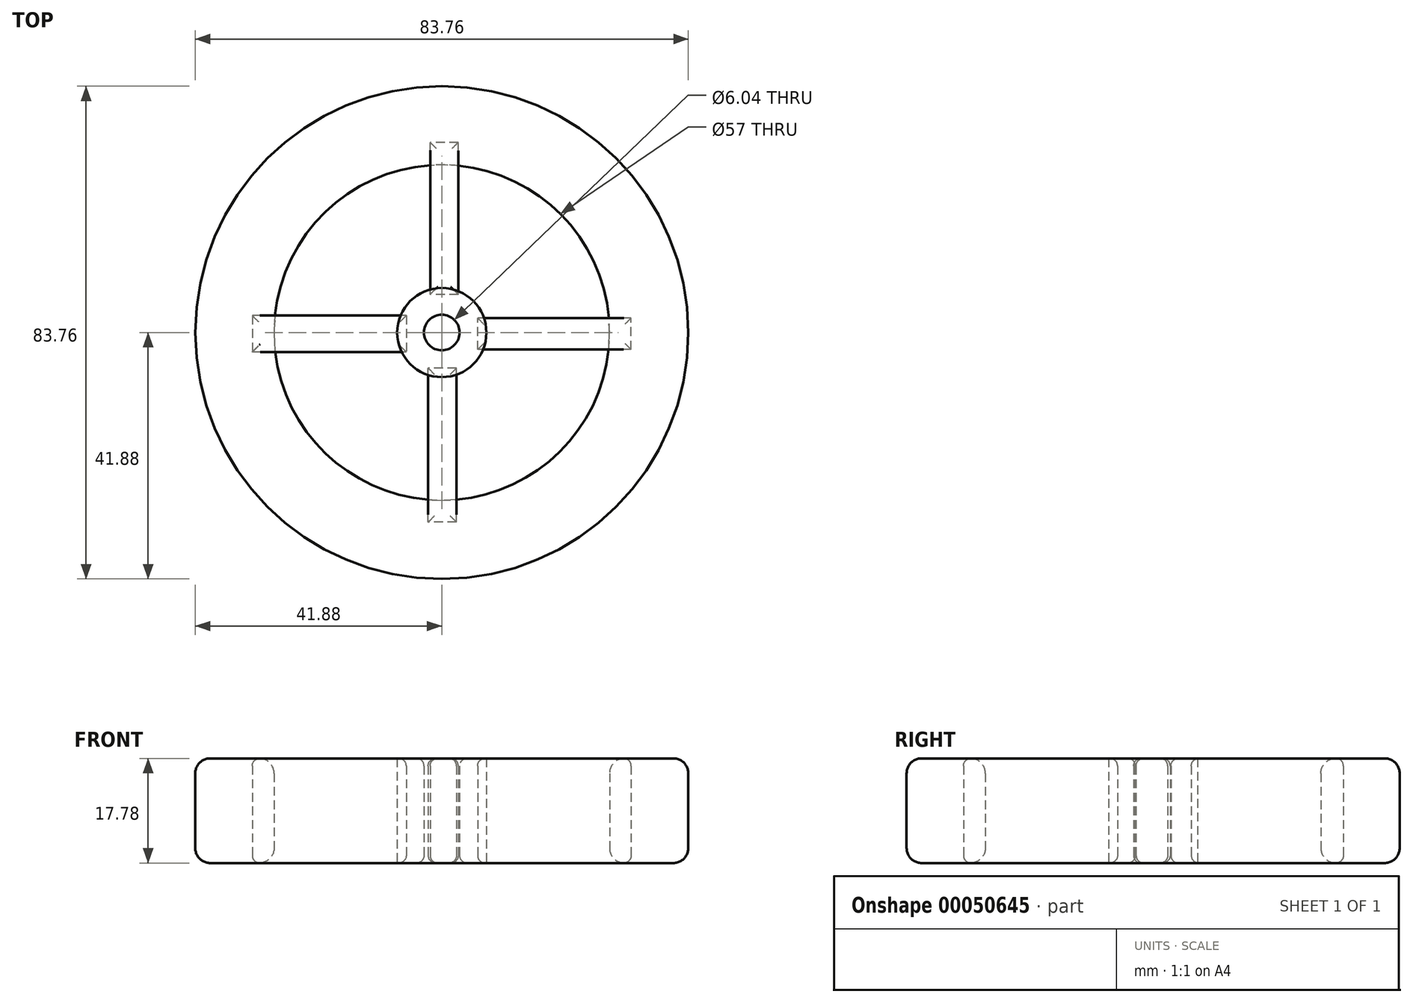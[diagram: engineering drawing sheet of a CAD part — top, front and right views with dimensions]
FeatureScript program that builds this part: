
annotation { "Feature Type Name" : "Feature", "Feature Type Description" : "" }
export const myFeature = defineFeature(function(context is Context, id is Id, definition is map)
    precondition{}
    {
        {
            var Q0;
            Q0=qCreatedBy(makeId("Top.planeOp"),FACE);
            var sketch = newSketch(context, id + "F0", { "sketchPlane" : qUnion([Q0])});
            skCircle(sketch, "E0", {"center": v(0, 0) * mm, "radius": 41.88 * mm});
            skCircle(sketch, "E1", {"center": v(0, 0) * mm, "radius": 22.29 * mm});
            skCircle(sketch, "E2", {"center": v(0, 0) * mm, "radius": 28.5 * mm});
            skSolve(sketch);
        }
        {
            var Q0;
            Q0=makeQuery(id+"F0.imprint","IMPRINT",FACE,{"disambiguationData":[TD([[makeQuery(id+"F0.imprint","IMPRINT",EDGE,{"derivedFrom":sQuery(id+"F0.wireOp",EDGE,"E0")}),1.0]])]});
            extrude(context, id + "F1", {"entities" : qUnion([Q0]), "depth" : 17.78 * mm});
        }
        {
            var Q0;
            Q0=qCreatedBy(makeId("Top.planeOp"),FACE);
            var sketch = newSketch(context, id + "F2", { "sketchPlane" : qUnion([Q0])});
            skCircle(sketch, "E3", {"center": v(0, 0) * mm, "radius": 7.58 * mm});
            skCircle(sketch, "E4", {"center": v(0, 0) * mm, "radius": 3.02 * mm});
            skSolve(sketch);
        }
        {
            var Q0;
            Q0=makeQuery(id+"F2.imprint","IMPRINT",FACE,{"disambiguationData":[TD([[makeQuery(id+"F2.imprint","IMPRINT",EDGE,{"derivedFrom":sQuery(id+"F2.wireOp",EDGE,"E3")}),1.0]])]});
            extrude(context, id + "F3", {"entities" : qUnion([Q0]), "depth" : 17.78 * mm});
        }
        {
            var Q0;
            Q0=qCreatedBy(makeId("Top.planeOp"),FACE);
            var sketch = newSketch(context, id + "F4", { "sketchPlane" : qUnion([Q0])});
            skLineSegment(sketch, "E5.bottom", {"start": v(2.5, -32.22) * mm, "end": v(-2.32, -32.22) * mm});
            skLineSegment(sketch, "E5.top", {"start": v(2.5, -6.05) * mm, "end": v(-2.32, -6.05) * mm});
            skLineSegment(sketch, "E5.left", {"start": v(2.5, -32.22) * mm, "end": v(2.5, -6.05) * mm});
            skLineSegment(sketch, "E5.right", {"start": v(-2.32, -32.22) * mm, "end": v(-2.32, -6.05) * mm});
            skSolve(sketch);
        }
        {
            var Q0;
            Q0=makeQuery(id+"F4.imprint","IMPRINT",FACE,{"disambiguationData":[TD([[makeQuery(id+"F4.imprint","IMPRINT",EDGE,{"derivedFrom":sQuery(id+"F4.wireOp",EDGE,"E5.bottom")}),-1.0]])]});
            extrude(context, id + "F5", {"entities" : qUnion([Q0]), "depth" : 17.78 * mm});
        }
        {
            var Q0;
            Q0=qCreatedBy(makeId("Top.planeOp"),FACE);
            var sketch = newSketch(context, id + "F6", { "sketchPlane" : qUnion([Q0])});
            skLineSegment(sketch, "E6.bottom", {"start": v(2.8, 6.48) * mm, "end": v(-1.98, 6.48) * mm});
            skLineSegment(sketch, "E6.top", {"start": v(2.8, 32.33) * mm, "end": v(-1.98, 32.33) * mm});
            skLineSegment(sketch, "E6.left", {"start": v(2.8, 6.48) * mm, "end": v(2.8, 32.33) * mm});
            skLineSegment(sketch, "E6.right", {"start": v(-1.98, 6.48) * mm, "end": v(-1.98, 32.33) * mm});
            skSolve(sketch);
        }
        {
            var Q0;
            Q0=makeQuery(id+"F6.imprint","IMPRINT",FACE,{"disambiguationData":[TD([[makeQuery(id+"F6.imprint","IMPRINT",EDGE,{"derivedFrom":sQuery(id+"F6.wireOp",EDGE,"E6.bottom")}),-1.0]])]});
            extrude(context, id + "F7", {"entities" : qUnion([Q0]), "depth" : 17.78 * mm});
        }
        {
            var Q0;
            Q0=qCreatedBy(makeId("Top.planeOp"),FACE);
            var sketch = newSketch(context, id + "F8", { "sketchPlane" : qUnion([Q0])});
            skLineSegment(sketch, "E7.bottom", {"start": v(-6.03, 2.9) * mm, "end": v(-32.2, 2.9) * mm});
            skLineSegment(sketch, "E7.top", {"start": v(-6.03, -3.3) * mm, "end": v(-32.2, -3.3) * mm});
            skLineSegment(sketch, "E7.left", {"start": v(-6.03, 2.9) * mm, "end": v(-6.03, -3.3) * mm});
            skLineSegment(sketch, "E7.right", {"start": v(-32.2, 2.9) * mm, "end": v(-32.2, -3.3) * mm});
            skSolve(sketch);
        }
        {
            var Q0;
            Q0=makeQuery(id+"F8.imprint","IMPRINT",FACE,{"disambiguationData":[TD([[makeQuery(id+"F8.imprint","IMPRINT",EDGE,{"derivedFrom":sQuery(id+"F8.wireOp",EDGE,"E7.bottom")}),1.0]])]});
            extrude(context, id + "F9", {"entities" : qUnion([Q0]), "depth" : 17.78 * mm});
        }
        {
            var Q0;
            Q0=qCreatedBy(makeId("Top.planeOp"),FACE);
            var sketch = newSketch(context, id + "F10", { "sketchPlane" : qUnion([Q0])});
            skLineSegment(sketch, "E8.bottom", {"start": v(32.17, -2.9) * mm, "end": v(6.08, -2.9) * mm});
            skLineSegment(sketch, "E8.top", {"start": v(32.17, 2.48) * mm, "end": v(6.08, 2.48) * mm});
            skLineSegment(sketch, "E8.left", {"start": v(32.17, -2.9) * mm, "end": v(32.17, 2.48) * mm});
            skLineSegment(sketch, "E8.right", {"start": v(6.08, -2.9) * mm, "end": v(6.08, 2.48) * mm});
            skSolve(sketch);
        }
        {
            var Q0;
            Q0=makeQuery(id+"F10.imprint","IMPRINT",FACE,{"disambiguationData":[TD([[makeQuery(id+"F10.imprint","IMPRINT",EDGE,{"derivedFrom":sQuery(id+"F10.wireOp",EDGE,"E8.bottom")}),-1.0]])]});
            extrude(context, id + "F11", {"entities" : qUnion([Q0]), "depth" : 17.78 * mm});
        }
        {
            var Q0;
            Q0=makeQuery(id+"F1.opExtrude","CAP_FACE",FACE,{"disambiguationData":[OSD([sQuery(id+"F0.wireOp",EDGE,"E0"),sQuery(id+"F0.wireOp",EDGE,"E2")])],"isStart":false});
            fillet(context, id + "F12", {"entities" : qUnion([Q0]), "radius" : 2.54 * mm, "tangentPropagation" : true, "allowEdgeOverflow" : false});
        }
        {
            var Q0;
            Q0=makeQuery(id+"F1.opExtrude","CAP_FACE",FACE,{"disambiguationData":[OSD([sQuery(id+"F0.wireOp",EDGE,"E0"),sQuery(id+"F0.wireOp",EDGE,"E2")])],"isStart":true});
            fillet(context, id + "F13", {"entities" : qUnion([Q0]), "radius" : 2.54 * mm, "tangentPropagation" : true, "allowEdgeOverflow" : false});
        }
        {
            var Q0;
            Q0=makeQuery(id+"F9.opExtrude","CAP_FACE",FACE,{"disambiguationData":[OSD([sQuery(id+"F8.wireOp",EDGE,"E7.bottom"),sQuery(id+"F8.wireOp",EDGE,"E7.top"),sQuery(id+"F8.wireOp",EDGE,"E7.left"),sQuery(id+"F8.wireOp",EDGE,"E7.right")])],"isStart":false});
            fillet(context, id + "F14", {"entities" : qUnion([Q0]), "radius" : 1.27 * mm, "tangentPropagation" : true, "allowEdgeOverflow" : false});
        }
        {
            var Q0;
            Q0=makeQuery(id+"F9.opExtrude","CAP_FACE",FACE,{"disambiguationData":[OSD([sQuery(id+"F8.wireOp",EDGE,"E7.bottom"),sQuery(id+"F8.wireOp",EDGE,"E7.top"),sQuery(id+"F8.wireOp",EDGE,"E7.left"),sQuery(id+"F8.wireOp",EDGE,"E7.right")])],"isStart":true});
            fillet(context, id + "F15", {"entities" : qUnion([Q0]), "radius" : 1.27 * mm, "tangentPropagation" : true, "allowEdgeOverflow" : false});
        }
        {
            var Q0;
            Q0=makeQuery(id+"F7.opExtrude","CAP_FACE",FACE,{"disambiguationData":[OSD([sQuery(id+"F6.wireOp",EDGE,"E6.bottom"),sQuery(id+"F6.wireOp",EDGE,"E6.top"),sQuery(id+"F6.wireOp",EDGE,"E6.left"),sQuery(id+"F6.wireOp",EDGE,"E6.right")])],"isStart":false});
            fillet(context, id + "F16", {"entities" : qUnion([Q0]), "radius" : 1.27 * mm, "tangentPropagation" : true, "allowEdgeOverflow" : false});
        }
        {
            var Q0;
            Q0=makeQuery(id+"F7.opExtrude","CAP_FACE",FACE,{"disambiguationData":[OSD([sQuery(id+"F6.wireOp",EDGE,"E6.bottom"),sQuery(id+"F6.wireOp",EDGE,"E6.top"),sQuery(id+"F6.wireOp",EDGE,"E6.left"),sQuery(id+"F6.wireOp",EDGE,"E6.right")])],"isStart":true});
            fillet(context, id + "F17", {"entities" : qUnion([Q0]), "radius" : 1.27 * mm, "tangentPropagation" : true, "allowEdgeOverflow" : false});
        }
        {
            var Q0;
            Q0=makeQuery(id+"F5.opExtrude","CAP_FACE",FACE,{"disambiguationData":[OSD([sQuery(id+"F4.wireOp",EDGE,"E5.bottom"),sQuery(id+"F4.wireOp",EDGE,"E5.top"),sQuery(id+"F4.wireOp",EDGE,"E5.left"),sQuery(id+"F4.wireOp",EDGE,"E5.right")])],"isStart":false});
            fillet(context, id + "F18", {"entities" : qUnion([Q0]), "radius" : 1.27 * mm, "tangentPropagation" : true, "allowEdgeOverflow" : false});
        }
        {
            var Q0;
            Q0=makeQuery(id+"F5.opExtrude","CAP_FACE",FACE,{"disambiguationData":[OSD([sQuery(id+"F4.wireOp",EDGE,"E5.bottom"),sQuery(id+"F4.wireOp",EDGE,"E5.top"),sQuery(id+"F4.wireOp",EDGE,"E5.left"),sQuery(id+"F4.wireOp",EDGE,"E5.right")])],"isStart":true});
            fillet(context, id + "F19", {"entities" : qUnion([Q0]), "radius" : 1.27 * mm, "tangentPropagation" : true, "allowEdgeOverflow" : false});
        }
        {
            var Q0;
            Q0=makeQuery(id+"F11.opExtrude","CAP_FACE",FACE,{"disambiguationData":[OSD([sQuery(id+"F10.wireOp",EDGE,"E8.bottom"),sQuery(id+"F10.wireOp",EDGE,"E8.top"),sQuery(id+"F10.wireOp",EDGE,"E8.left"),sQuery(id+"F10.wireOp",EDGE,"E8.right")])],"isStart":true});
            fillet(context, id + "F20", {"entities" : qUnion([Q0]), "radius" : 1.27 * mm, "tangentPropagation" : true, "allowEdgeOverflow" : false});
        }
        {
            var Q0;
            Q0=makeQuery(id+"F11.opExtrude","CAP_FACE",FACE,{"disambiguationData":[OSD([sQuery(id+"F10.wireOp",EDGE,"E8.bottom"),sQuery(id+"F10.wireOp",EDGE,"E8.top"),sQuery(id+"F10.wireOp",EDGE,"E8.left"),sQuery(id+"F10.wireOp",EDGE,"E8.right")])],"isStart":false});
            fillet(context, id + "F21", {"entities" : qUnion([Q0]), "radius" : 1.27 * mm, "tangentPropagation" : true, "allowEdgeOverflow" : false});
        }
        {
            var Q0;
            Q0=makeQuery(id+"F3.opExtrude","CAP_EDGE",EDGE,{"disambiguationData":[OSD([sQuery(id+"F2.wireOp",EDGE,"E4")])],"isStart":false});
            fillet(context, id + "F22", {"entities" : qUnion([Q0]), "radius" : 1.27 * mm, "tangentPropagation" : true, "allowEdgeOverflow" : false});
        }
        {
            var Q0;
            Q0=makeQuery(id+"F3.opExtrude","CAP_EDGE",EDGE,{"disambiguationData":[OSD([sQuery(id+"F2.wireOp",EDGE,"E4")])],"isStart":true});
            fillet(context, id + "F23", {"entities" : qUnion([Q0]), "radius" : 1.27 * mm, "tangentPropagation" : true, "allowEdgeOverflow" : false});
        }
    });
